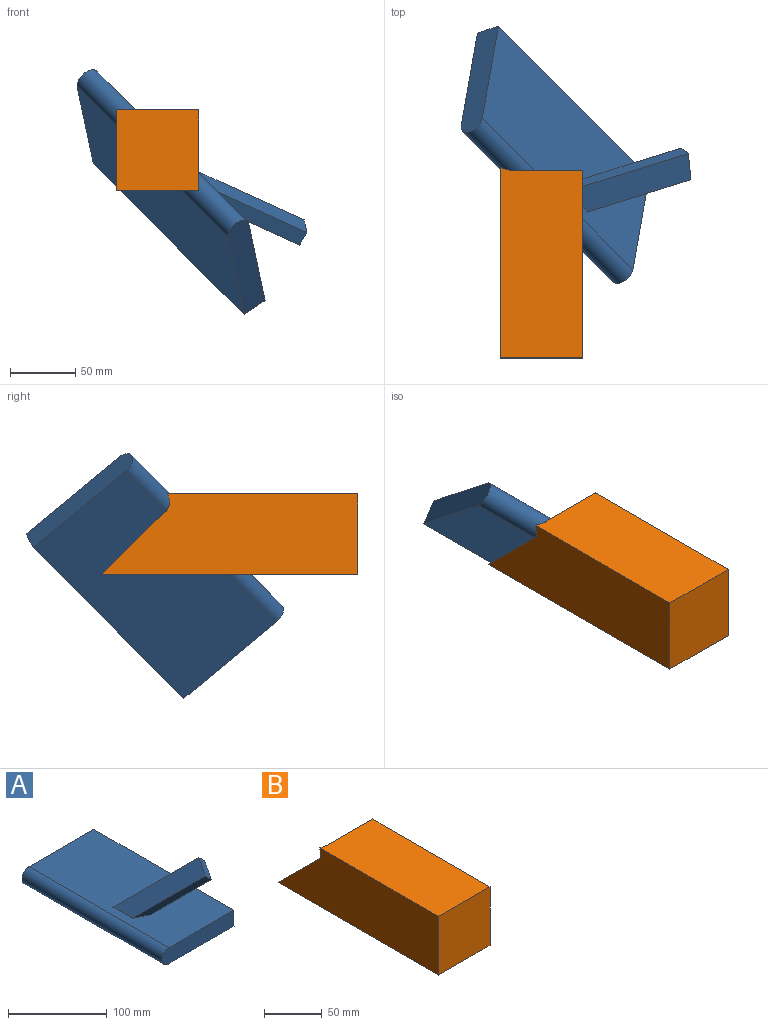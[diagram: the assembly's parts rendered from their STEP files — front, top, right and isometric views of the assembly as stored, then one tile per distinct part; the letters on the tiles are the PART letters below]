
ASSEMBLY  parts=2 mates=1
PART A: 11 faces, bbox 102.9x200x81.4 mm
  f0: cylinder r=10mm len=200mm, axis (0,1,0), area 6283.2mm2, adj f1,f2,f3,f4
  f1: plane 102.9x20mm, normal (0,-1,0), area 2012.4mm2, adj f0,f3,f4,f5
  f2: plane 102.9x20mm, normal (0,1,0), area 2012.4mm2, adj f0,f3,f4,f5
  f3: plane 200x92.63mm, normal (0,0,1), area 18060.4mm2, adj f0,f1,f2,f5,f6,f8,f9,f10
  f4: plane 200x92.9mm, normal (0,0,-1), area 18580.6mm2, adj f0,f1,f2,f5
  f5: plane 200x20mm, normal (1,0,0.01), area 4000.4mm2, adj f1,f2,f3,f4
  f6: plane 69.86x61.38mm, normal (0.41,0.82,0.41), area 1187.5mm2, adj f3,f7,f9,f10
  f7: plane 18.28x17.63mm, normal (0.58,-0.58,0.58), area 268.7mm2, adj f6,f8,f9,f10
  f8: plane 60.72x52.24mm, normal (-0.41,-0.82,-0.41), area 997.5mm2, adj f3,f7,f9,f10
  f9: plane 71.18x52.89mm, normal (0.71,0,-0.71), area 1874.2mm2, adj f3,f6,f7,f8
  f10: plane 79.66x61.38mm, normal (-0.71,0,0.71), area 2203.3mm2, adj f3,f6,f7,f8
PART B: 8 faces, bbox 70.7x196.5x73.7 mm
  f0: plane 196.51x62.04mm, normal (-1,0,0), area 10320.3mm2, adj f1,f2,f4,f5,f6
  f1: plane 196.51x62.98mm, normal (0,0,-1), area 8474.9mm2, adj f0,f2,f3,f5,f6
  f2: cylinder r=10mm len=73.66mm, axis (0.58,-0.58,-0.58), area 1545.2mm2, adj f0,f1,f3,f4,f6,f7
  f3: plane 143.88x62.04mm, normal (1,0,0), area 7005.3mm2, adj f1,f2,f4,f5,f7
  f4: plane 146.01x62.98mm, normal (0,0,1), area 9067.3mm2, adj f0,f2,f3,f5,f7
  f5: plane 62.98x62.04mm, normal (0,-1,0), area 3907.3mm2, adj f0,f1,f3,f4
  f6: plane 100.53x50.26mm, normal (0.82,0.41,0.41), area 3094.1mm2, adj f0,f1,f2
  f7: plane 55.44x55.44mm, normal (0,0.71,-0.71), area 2173.3mm2, adj f2,f3,f4
PLACE A rot(axis=(0.15,0.72,0.68),83.4deg) t=(35.57,122.92,26.94)mm
PLACE B t=(31.49,127,31.02)mm
MATE revolute A.f0 <-> B.f2  axis (-0.58,0.58,0.58) through (35.57,122.92,26.94)mm
